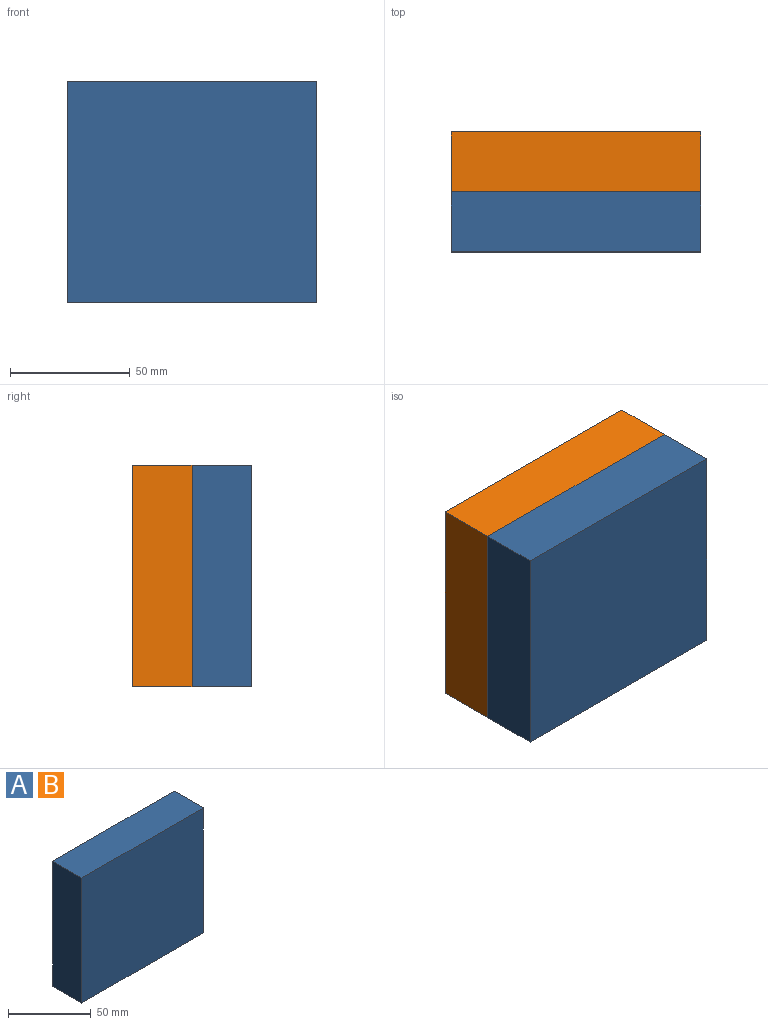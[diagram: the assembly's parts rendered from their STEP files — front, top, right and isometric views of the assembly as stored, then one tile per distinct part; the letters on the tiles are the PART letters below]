
ASSEMBLY  parts=2 mates=1
PART A: 6 faces, bbox 104.3x25x92.7 mm
  f0: plane 92.72x25mm, normal (-1,0,0), area 2317.9mm2, adj f1,f3,f4,f5
  f1: plane 104.26x25mm, normal (0,0,-1), area 2606.4mm2, adj f0,f2,f4,f5
  f2: plane 92.72x25mm, normal (1,0,0), area 2317.9mm2, adj f1,f3,f4,f5
  f3: plane 104.26x25mm, normal (0,0,1), area 2606.4mm2, adj f0,f2,f4,f5
  f4: plane 104.26x92.72mm, normal (0,-1,0), area 9666.3mm2, adj f0,f1,f2,f3
  f5: plane 104.26x92.72mm, normal (0,1,0), area 9666.3mm2, adj f0,f1,f2,f3
PART B: same geometry as A
PLACE A rot(axis=(1,0,0),180deg) t=(-74.19,-100.69,26.58)mm
PLACE B t=(-74.19,-50.69,-11.79)mm
MATE cylindrical A.f4 <-> B.f4  axis (0,1,0) through (-82.38,-75.69,7.4)mm
